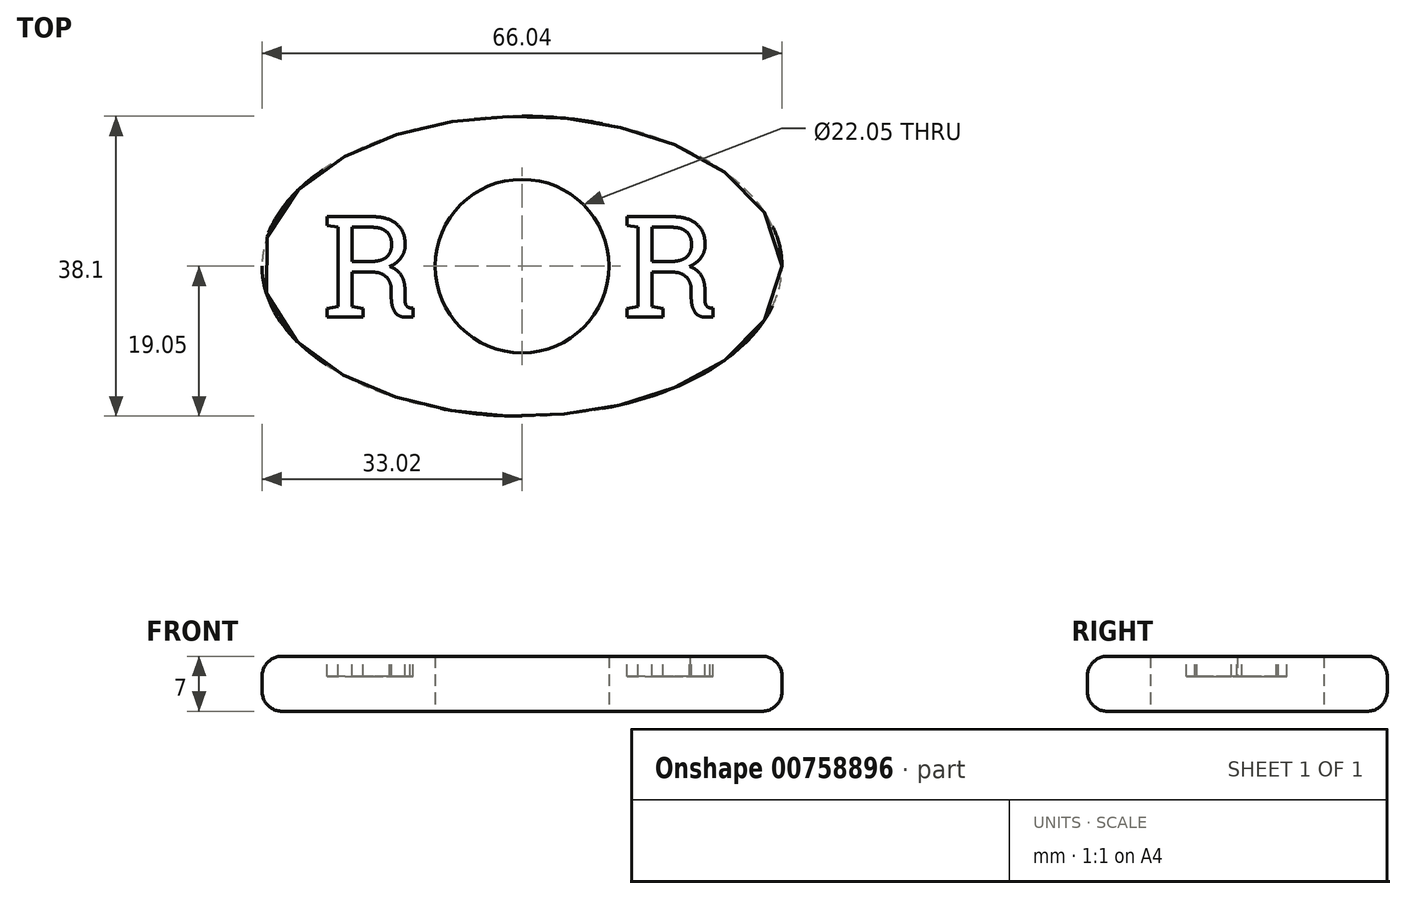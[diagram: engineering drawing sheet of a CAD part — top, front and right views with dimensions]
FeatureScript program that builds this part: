
annotation { "Feature Type Name" : "Feature", "Feature Type Description" : "" }
export const myFeature = defineFeature(function(context is Context, id is Id, definition is map)
    precondition{}
    {
        {
            var Q0;
            Q0=qCreatedBy(makeId("Top.planeOp"),FACE);
            var sketch = newSketch(context, id + "F0", { "sketchPlane" : qUnion([Q0])});
            skEllipse(sketch, "E0", {"center": v(0, 0) * mm, "majorRadius": 33.02 * mm, "minorRadius": 19.05 * mm, "majorAxis": v(1, 0)});
            skCircle(sketch, "E1", {"center": v(0, 0) * mm, "radius": 11.03 * mm});
            skLineSegment(sketch, "E2", {"start": v(-33.02, 0) * mm, "end": v(33.02, 0) * mm, "construction": true});
            skLineSegment(sketch, "E3", {"start": v(0, 19.05) * mm, "end": v(0, -19.05) * mm, "construction": true});
            skSolve(sketch);
        }
        {
            var Q0;
            Q0=makeQuery(id+"F0.imprint","IMPRINT",FACE,{"disambiguationData":[TD([[makeQuery(id+"F0.imprint","IMPRINT",EDGE,{"derivedFrom":sQuery(id+"F0.wireOp",EDGE,"E0")}),1.0]])]});
            extrude(context, id + "F1", {"entities" : qUnion([Q0]), "depth" : 7 * mm, "offsetDistance" : 25.4 * mm});
        }
        {
            var Q0;
            Q0=makeQuery(id+"F1.opExtrude","CAP_EDGE",EDGE,{"disambiguationData":[OSD([sQuery(id+"F0.wireOp",EDGE,"E0")])],"isStart":false});
            var Q1;
            Q1=makeQuery(id+"F1.opExtrude","CAP_EDGE",EDGE,{"disambiguationData":[OSD([sQuery(id+"F0.wireOp",EDGE,"E0")])],"isStart":true});
            fillet(context, id + "F2", {"entities" : qUnion([Q0, Q1]), "radius" : 2.54 * mm, "tangentPropagation" : true, "allowEdgeOverflow" : false});
        }
        {
            var Q0;
            Q0=makeQuery(id+"F1.opExtrude","CAP_FACE",FACE,{"disambiguationData":[OSD([sQuery(id+"F0.wireOp",EDGE,"E0"),sQuery(id+"F0.wireOp",EDGE,"E1")])],"isStart":false});
            var sketch = newSketch(context, id + "F3", { "sketchPlane" : qUnion([Q0])});
            skSolve(sketch);
        }
        {
            var Q0;
            {var subQ0=sQuery(id+"F0.wireOp",EDGE,"E1");Q0=makeQuery(id+"F3.imprint","IMPRINT",FACE,{"disambiguationData":[TD([[makeQuery(id+"F3.imprint","IMPRINT",EDGE,{"derivedFrom":makeQuery(id+"F1.opExtrude","CAP_EDGE",EDGE,{"disambiguationData":[OSD([subQ0])],"isStart":false})}),-1.0]])]});}
            var sketch = newSketch(context, id + "F4", { "sketchPlane" : qUnion([Q0])});
            skText(sketch, "E4", { "text": "R", "fontName": "RobotoSlab-Regular.ttf"});
            skText(sketch, "E5", { "text": "R", "fontName": "RobotoSlab-Regular.ttf"});
            skLineSegment(sketch, "E6", {"start": v(0, 0) * mm, "end": v(-25.4, 0) * mm, "construction": true});
            skLineSegment(sketch, "E7", {"start": v(0, 0) * mm, "end": v(25.4, 0) * mm, "construction": true});
            skLineSegment(sketch, "E8", {"start": v(-25.4, 0) * mm, "end": v(-12.7, 0) * mm, "construction": true});
            skLineSegment(sketch, "E9", {"start": v(12.7, 0) * mm, "end": v(25.4, 0) * mm});
            skPoint(sketch, "E10", {"position": v(19.05, 0) * mm});
            skLineSegment(sketch, "E11", {"start": v(12.7, 0) * mm, "end": v(25.4, 0) * mm, "construction": true});
            skPoint(sketch, "E12", {"position": v(-19.05, 0) * mm});
            const initialGuessF4  = {"E4": [-0.0254, -0.00648, 1, 0, 0.01295], "E5": [0.0127, -0.00648, 1, 0, 0.01295]};
            skSetInitialGuess(sketch, initialGuessF4);
            skSolve(sketch);
        }
        {
            var Q0;
            Q0=qSketchRegion(id+"F4",true);
            extrude(context, id + "F5", {"entities" : qUnion([Q0]), "operationType" : NewBodyOperationType.REMOVE, "oppositeDirection" : true, "depth" : 2.54 * mm, "offsetDistance" : 25.4 * mm});
        }
    });
